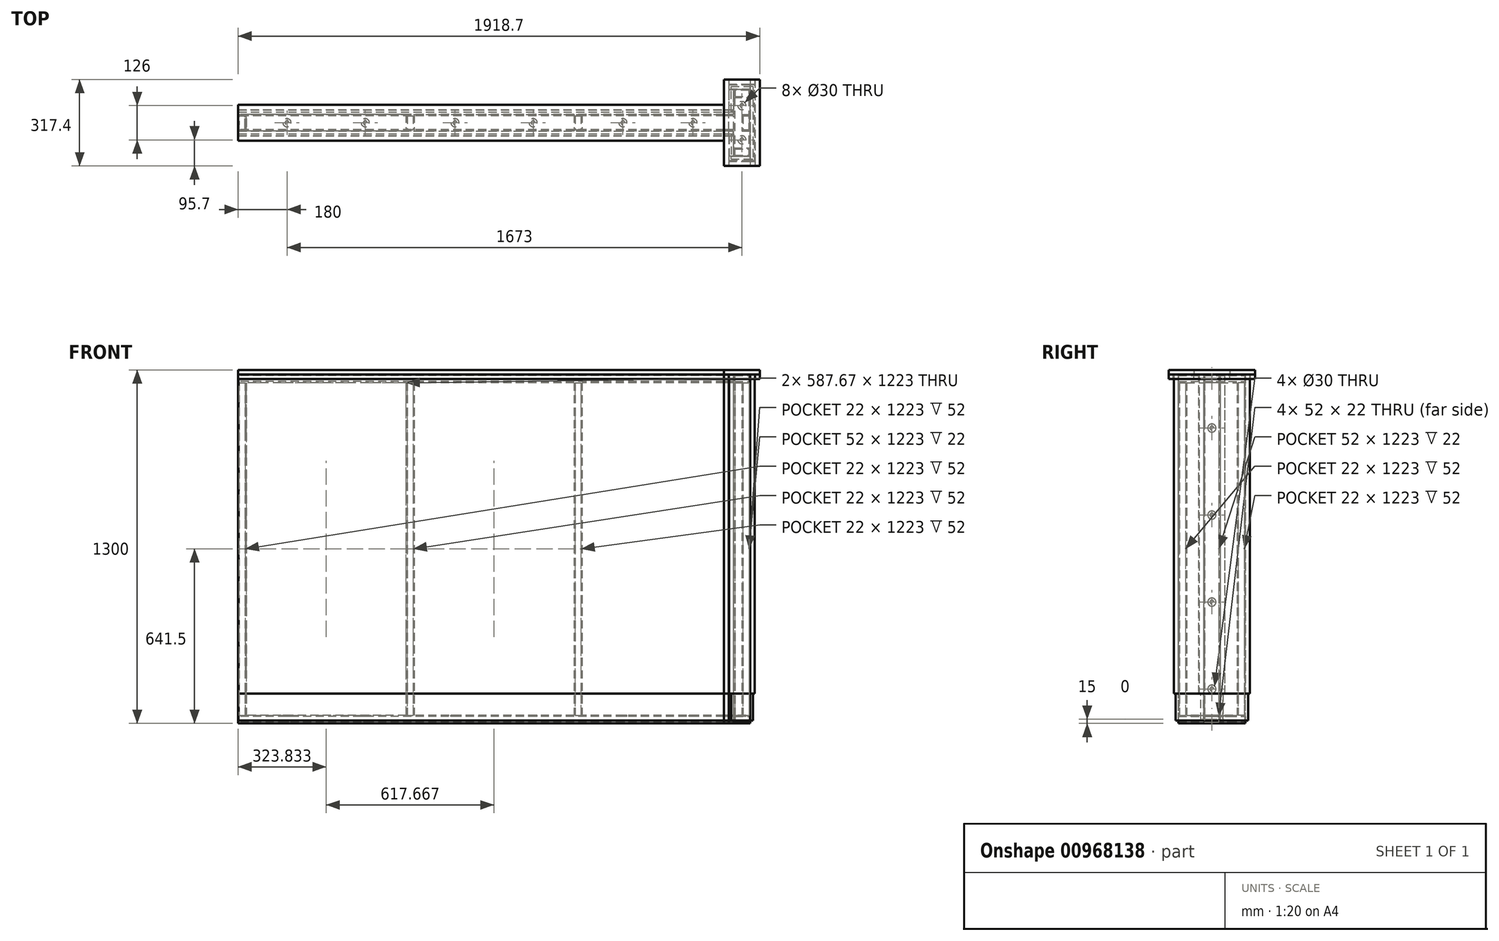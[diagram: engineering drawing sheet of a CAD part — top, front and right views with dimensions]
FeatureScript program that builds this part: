
annotation { "Feature Type Name" : "Feature", "Feature Type Description" : "" }
export const myFeature = defineFeature(function(context is Context, id is Id, definition is map)
    precondition{}
    {
        {
            var Q0;
            Q0=qCreatedBy(makeId("Right.planeOp"),FACE);
            var sketch = newSketch(context, id + "F0", { "sketchPlane" : qUnion([Q0])});
            skLineSegment(sketch, "E0.bottom", {"start": v(-30, 30) * mm, "end": v(30, 30) * mm});
            skLineSegment(sketch, "E0.top", {"start": v(-30, 0) * mm, "end": v(30, 0) * mm});
            skLineSegment(sketch, "E0.left", {"start": v(-30, 30) * mm, "end": v(-30, 0) * mm});
            skLineSegment(sketch, "E0.right", {"start": v(30, 30) * mm, "end": v(30, 0) * mm});
            skLineSegment(sketch, "E1.bottom", {"start": v(-26, 26) * mm, "end": v(26, 26) * mm});
            skLineSegment(sketch, "E1.top", {"start": v(-26, 4) * mm, "end": v(26, 4) * mm});
            skLineSegment(sketch, "E1.left", {"start": v(-26, 26) * mm, "end": v(-26, 4) * mm});
            skLineSegment(sketch, "E1.right", {"start": v(26, 26) * mm, "end": v(26, 4) * mm});
            skLineSegment(sketch, "E2.bottom", {"start": v(-30, 1283) * mm, "end": v(30, 1283) * mm});
            skLineSegment(sketch, "E2.top", {"start": v(-30, 1253) * mm, "end": v(30, 1253) * mm});
            skLineSegment(sketch, "E2.left", {"start": v(-30, 1283) * mm, "end": v(-30, 1253) * mm});
            skLineSegment(sketch, "E2.right", {"start": v(30, 1283) * mm, "end": v(30, 1253) * mm});
            skLineSegment(sketch, "E3.bottom", {"start": v(-26, 1279) * mm, "end": v(26, 1279) * mm});
            skLineSegment(sketch, "E3.top", {"start": v(-26, 1257) * mm, "end": v(26, 1257) * mm});
            skLineSegment(sketch, "E3.left", {"start": v(-26, 1279) * mm, "end": v(-26, 1257) * mm});
            skLineSegment(sketch, "E3.right", {"start": v(26, 1279) * mm, "end": v(26, 1257) * mm});
            skLineSegment(sketch, "E4", {"start": v(0, 1283) * mm, "end": v(0, 1279) * mm, "construction": true});
            skLineSegment(sketch, "E5", {"start": v(-30, 1268) * mm, "end": v(-26, 1268) * mm, "construction": true});
            skLineSegment(sketch, "E6", {"start": v(0, 1257) * mm, "end": v(0, 1253) * mm, "construction": true});
            skLineSegment(sketch, "E7", {"start": v(30, 1268) * mm, "end": v(26, 1268) * mm, "construction": true});
            skLineSegment(sketch, "E8", {"start": v(0, 30) * mm, "end": v(0, 26) * mm, "construction": true});
            skLineSegment(sketch, "E9", {"start": v(26, 15) * mm, "end": v(30, 15) * mm, "construction": true});
            skLineSegment(sketch, "E10", {"start": v(0, 0) * mm, "end": v(0, 4) * mm, "construction": true});
            skPoint(sketch, "E10.endSnap0", {"position": v(0, 4) * mm});
            skLineSegment(sketch, "E11", {"start": v(-26, 15) * mm, "end": v(-30, 15) * mm, "construction": true});
            skSolve(sketch);
        }
        {
            var Q0;
            Q0 = qSketchRegion(id + "F0", true);
            extrude(context, id + "F1", {"entities" : qUnion([Q0]), "depth" : (1900 - 17 - 60) * mm, "offsetDistance" : 25 * mm});
        }
        {
            var Q0;
            Q0=makeQuery(id+"F1.opExtrude","SWEPT_FACE",FACE,{"disambiguationData":[OSD([sQuery(id+"F0.wireOp",EDGE,"E0.bottom")])]});
            var sketch = newSketch(context, id + "F2", { "sketchPlane" : qUnion([Q0])});
            skLineSegment(sketch, "E12.bottom", {"start": v(0, -30) * mm, "end": v(30, -30) * mm});
            skLineSegment(sketch, "E12.top", {"start": v(0, 30) * mm, "end": v(30, 30) * mm});
            skLineSegment(sketch, "E12.left", {"start": v(0, -30) * mm, "end": v(0, 30) * mm});
            skLineSegment(sketch, "E12.right", {"start": v(30, -30) * mm, "end": v(30, 30) * mm});
            skLineSegment(sketch, "E13.bottom", {"start": v(4, -26) * mm, "end": v(26, -26) * mm});
            skLineSegment(sketch, "E13.top", {"start": v(4, 26) * mm, "end": v(26, 26) * mm});
            skLineSegment(sketch, "E13.left", {"start": v(4, -26) * mm, "end": v(4, 26) * mm});
            skLineSegment(sketch, "E13.right", {"start": v(26, -26) * mm, "end": v(26, 26) * mm});
            skLineSegment(sketch, "E14", {"start": v(15, -30) * mm, "end": v(15, -26) * mm, "construction": true});
            skLineSegment(sketch, "E15", {"start": v(30, 0) * mm, "end": v(26, 0) * mm, "construction": true});
            skLineSegment(sketch, "E16", {"start": v(15, 30) * mm, "end": v(15, 26) * mm, "construction": true});
            skLineSegment(sketch, "E17", {"start": v(4, 0) * mm, "end": v(0, 0) * mm, "construction": true});
            skSolve(sketch);
        }
        {
            var Q0;
            Q0 = qSketchRegion(id + "F2", true);
            extrude(context, id + "F3", {"entities" : qUnion([Q0]), "endBound" : BoundingType.UP_TO_NEXT, "depth" : 25 * mm, "offsetDistance" : 25 * mm});
        }
        {
            var Q0;
            Q0=qCreatedBy(makeId("Front.planeOp"),FACE);
            var sketch = newSketch(context, id + "F4", { "sketchPlane" : qUnion([Q0])});
            skLineSegment(sketch, "E18.bottom", {"start": v(1823, 1253) * mm, "end": v(1883, 1253) * mm});
            skLineSegment(sketch, "E18.top", {"start": v(1823, 1283) * mm, "end": v(1883, 1283) * mm});
            skLineSegment(sketch, "E18.left", {"start": v(1823, 1253) * mm, "end": v(1823, 1283) * mm});
            skLineSegment(sketch, "E18.right", {"start": v(1883, 1253) * mm, "end": v(1883, 1283) * mm});
            skLineSegment(sketch, "E19.bottom", {"start": v(1827, 1257) * mm, "end": v(1879, 1257) * mm});
            skLineSegment(sketch, "E19.top", {"start": v(1827, 1279) * mm, "end": v(1879, 1279) * mm});
            skLineSegment(sketch, "E19.left", {"start": v(1827, 1257) * mm, "end": v(1827, 1279) * mm});
            skLineSegment(sketch, "E19.right", {"start": v(1879, 1257) * mm, "end": v(1879, 1279) * mm});
            skLineSegment(sketch, "E20.bottom", {"start": v(1823, 30) * mm, "end": v(1883, 30) * mm});
            skLineSegment(sketch, "E20.top", {"start": v(1823, 0) * mm, "end": v(1883, 0) * mm});
            skLineSegment(sketch, "E20.left", {"start": v(1823, 30) * mm, "end": v(1823, 0) * mm});
            skLineSegment(sketch, "E20.right", {"start": v(1883, 30) * mm, "end": v(1883, 0) * mm});
            skLineSegment(sketch, "E21.bottom", {"start": v(1827, 26) * mm, "end": v(1879, 26) * mm});
            skLineSegment(sketch, "E21.top", {"start": v(1827, 4) * mm, "end": v(1879, 4) * mm});
            skLineSegment(sketch, "E21.left", {"start": v(1827, 26) * mm, "end": v(1827, 4) * mm});
            skLineSegment(sketch, "E21.right", {"start": v(1879, 26) * mm, "end": v(1879, 4) * mm});
            skLineSegment(sketch, "E22", {"start": v(1853, 30) * mm, "end": v(1853, 26) * mm, "construction": true});
            skLineSegment(sketch, "E23", {"start": v(1827, 15) * mm, "end": v(1823, 15) * mm, "construction": true});
            skLineSegment(sketch, "E24", {"start": v(1853, 4) * mm, "end": v(1853, 0) * mm, "construction": true});
            skLineSegment(sketch, "E25", {"start": v(1879, 15) * mm, "end": v(1883, 15) * mm, "construction": true});
            skLineSegment(sketch, "E26", {"start": v(1853, 1283) * mm, "end": v(1853, 1279) * mm, "construction": true});
            skLineSegment(sketch, "E27", {"start": v(1823, 1268) * mm, "end": v(1827, 1268) * mm, "construction": true});
            skLineSegment(sketch, "E28", {"start": v(1853, 1253) * mm, "end": v(1853, 1257) * mm, "construction": true});
            skPoint(sketch, "E28.startSnap0", {"position": v(1853, 1257) * mm});
            skLineSegment(sketch, "E29", {"start": v(1879, 1268) * mm, "end": v(1883, 1268) * mm, "construction": true});
            skSolve(sketch);
        }
        {
            var Q0;
            Q0 = qSketchRegion(id + "F4", true);
            extrude(context, id + "F5", {"entities" : qUnion([Q0]), "endBound" : BoundingType.SYMMETRIC, "depth" : (320 - 17 - 17 - 20 - 20) * mm, "offsetDistance" : 25 * mm});
        }
        {
            var Q0;
            Q0=makeQuery(id+"F5.opExtrude","SWEPT_FACE",FACE,{"disambiguationData":[OSD([sQuery(id+"F4.wireOp",EDGE,"E20.bottom")])]});
            var sketch = newSketch(context, id + "F6", { "sketchPlane" : qUnion([Q0])});
            skLineSegment(sketch, "E30.bottom", {"start": v(1883, 123) * mm, "end": v(1823, 123) * mm});
            skLineSegment(sketch, "E30.top", {"start": v(1883, 123) * mm, "end": v(1823, 123) * mm});
            skLineSegment(sketch, "E30.left", {"start": v(1883, 123) * mm, "end": v(1883, 123) * mm});
            skLineSegment(sketch, "E30.right", {"start": v(1823, 123) * mm, "end": v(1823, 123) * mm});
            skLineSegment(sketch, "E31.bottom", {"start": v(1823, 123) * mm, "end": v(1883, 123) * mm});
            skLineSegment(sketch, "E31.top", {"start": v(1823, 93) * mm, "end": v(1883, 93) * mm});
            skLineSegment(sketch, "E31.left", {"start": v(1823, 123) * mm, "end": v(1823, 93) * mm});
            skLineSegment(sketch, "E31.right", {"start": v(1883, 123) * mm, "end": v(1883, 93) * mm});
            skLineSegment(sketch, "E32.bottom", {"start": v(1883, -123) * mm, "end": v(1823, -123) * mm});
            skLineSegment(sketch, "E32.top", {"start": v(1883, -123) * mm, "end": v(1823, -123) * mm});
            skLineSegment(sketch, "E32.left", {"start": v(1883, -123) * mm, "end": v(1883, -123) * mm});
            skLineSegment(sketch, "E32.right", {"start": v(1823, -123) * mm, "end": v(1823, -123) * mm});
            skLineSegment(sketch, "E33.bottom", {"start": v(1823, -123) * mm, "end": v(1883, -123) * mm});
            skLineSegment(sketch, "E33.top", {"start": v(1823, -93) * mm, "end": v(1883, -93) * mm});
            skLineSegment(sketch, "E33.left", {"start": v(1823, -123) * mm, "end": v(1823, -93) * mm});
            skLineSegment(sketch, "E33.right", {"start": v(1883, -123) * mm, "end": v(1883, -93) * mm});
            skLineSegment(sketch, "E34.bottom", {"start": v(1853, 30) * mm, "end": v(1883, 30) * mm});
            skLineSegment(sketch, "E34.top", {"start": v(1853, -30) * mm, "end": v(1883, -30) * mm});
            skLineSegment(sketch, "E34.left", {"start": v(1853, 30) * mm, "end": v(1853, -30) * mm});
            skLineSegment(sketch, "E34.right", {"start": v(1883, 30) * mm, "end": v(1883, -30) * mm});
            skLineSegment(sketch, "E35.0", {"start": v(1857, 26) * mm, "end": v(1879, 26) * mm});
            skLineSegment(sketch, "E35.1", {"start": v(1857, 26) * mm, "end": v(1857, -26) * mm});
            skLineSegment(sketch, "E35.2", {"start": v(1857, -26) * mm, "end": v(1879, -26) * mm});
            skLineSegment(sketch, "E35.3", {"start": v(1879, 26) * mm, "end": v(1879, -26) * mm});
            skLineSegment(sketch, "E36.0", {"start": v(1879, 119) * mm, "end": v(1879, 97) * mm});
            skLineSegment(sketch, "E36.1", {"start": v(1879, 119) * mm, "end": v(1827, 119) * mm});
            skLineSegment(sketch, "E36.2", {"start": v(1827, 119) * mm, "end": v(1827, 97) * mm});
            skLineSegment(sketch, "E36.3", {"start": v(1827, 97) * mm, "end": v(1879, 97) * mm});
            skLineSegment(sketch, "E37.0", {"start": v(1827, -97) * mm, "end": v(1879, -97) * mm});
            skLineSegment(sketch, "E37.1", {"start": v(1827, -119) * mm, "end": v(1827, -97) * mm});
            skLineSegment(sketch, "E37.2", {"start": v(1827, -119) * mm, "end": v(1879, -119) * mm});
            skLineSegment(sketch, "E37.3", {"start": v(1879, -119) * mm, "end": v(1879, -97) * mm});
            skLineSegment(sketch, "E38.1.0.0", {"start": v(1235.33, 30) * mm, "end": v(1265.33, 30) * mm});
            skLineSegment(sketch, "E38.1.0.1", {"start": v(1235.33, 30) * mm, "end": v(1235.33, -30) * mm});
            skLineSegment(sketch, "E38.1.0.2", {"start": v(1235.33, -30) * mm, "end": v(1265.33, -30) * mm});
            skLineSegment(sketch, "E38.1.0.3", {"start": v(1239.33, 26) * mm, "end": v(1239.33, -26) * mm});
            skLineSegment(sketch, "E38.1.0.4", {"start": v(1239.33, 26) * mm, "end": v(1261.33, 26) * mm});
            skLineSegment(sketch, "E38.1.0.5", {"start": v(1265.33, 30) * mm, "end": v(1265.33, -30) * mm});
            skLineSegment(sketch, "E38.1.0.6", {"start": v(1261.33, 26) * mm, "end": v(1261.33, -26) * mm});
            skLineSegment(sketch, "E38.1.0.7", {"start": v(1239.33, -26) * mm, "end": v(1261.33, -26) * mm});
            skLineSegment(sketch, "E38.direction1", {"start": v(1853, 30) * mm, "end": v(1235.33, 30) * mm, "construction": true});
            skLineSegment(sketch, "E39.0.2.0", {"start": v(617.67, 30) * mm, "end": v(647.67, 30) * mm});
            skLineSegment(sketch, "E39.3.2.0", {"start": v(617.67, 30) * mm, "end": v(617.67, -30) * mm});
            skLineSegment(sketch, "E39.6.2.0", {"start": v(617.67, -30) * mm, "end": v(647.67, -30) * mm});
            skLineSegment(sketch, "E39.9.2.0", {"start": v(621.67, 26) * mm, "end": v(621.67, -26) * mm});
            skLineSegment(sketch, "E39.12.2.0", {"start": v(621.67, 26) * mm, "end": v(643.67, 26) * mm});
            skLineSegment(sketch, "E39.15.2.0", {"start": v(647.67, 30) * mm, "end": v(647.67, -30) * mm});
            skLineSegment(sketch, "E39.18.2.0", {"start": v(643.67, 26) * mm, "end": v(643.67, -26) * mm});
            skLineSegment(sketch, "E39.21.2.0", {"start": v(621.67, -26) * mm, "end": v(643.67, -26) * mm});
            skLineSegment(sketch, "E40", {"start": v(617.67, 0) * mm, "end": v(30, 0) * mm, "construction": true});
            skLineSegment(sketch, "E41", {"start": v(647.67, 0) * mm, "end": v(1235.33, 0) * mm, "construction": true});
            skLineSegment(sketch, "E42", {"start": v(1265.33, 0) * mm, "end": v(1853, 0) * mm, "construction": true});
            skSolve(sketch);
        }
        {
            var Q0;
            Q0 = qSketchRegion(id + "F6", true);
            extrude(context, id + "F7", {"entities" : qUnion([Q0]), "endBound" : BoundingType.UP_TO_NEXT, "depth" : 25 * mm, "offsetDistance" : 25 * mm});
        }
        {
            var Q0;
            Q0=makeQuery(id+"F1.opExtrude","SWEPT_FACE",FACE,{"disambiguationData":[OSD([sQuery(id+"F0.wireOp",EDGE,"E2.left")])]});
            cPlane(context, id + "F8", {"entities" : qUnion([Q0]), "cplaneType" : CPlaneType.OFFSET, "offset" : 0 * mm, "width" : 150 * mm, "height" : 150 * mm});
        }
        {
            var Q0;
            Q0=qCreatedBy(id+"F8.planeOp",FACE);
            var sketch = newSketch(context, id + "F9", { "sketchPlane" : qUnion([Q0])});
            skLineSegment(sketch, "E43.bottom", {"start": v(1.3, 1281.7) * mm, "end": v(1821.7, 1281.7) * mm});
            skLineSegment(sketch, "E43.top", {"start": v(1.3, 110) * mm, "end": v(1821.7, 110) * mm});
            skLineSegment(sketch, "E43.left", {"start": v(1.3, 1281.7) * mm, "end": v(1.3, 110) * mm});
            skLineSegment(sketch, "E43.right", {"start": v(1821.7, 1281.7) * mm, "end": v(1821.7, 110) * mm});
            skLineSegment(sketch, "E44", {"start": v(911.5, 1281.7) * mm, "end": v(911.5, 1283) * mm, "construction": true});
            skLineSegment(sketch, "E45", {"start": v(1821.7, 695.85) * mm, "end": v(1823, 695.85) * mm, "construction": true});
            skLineSegment(sketch, "E46", {"start": v(1.3, 641.5) * mm, "end": v(0, 641.5) * mm, "construction": true});
            skSolve(sketch);
        }
        {
            var Q0;
            Q0 = qSketchRegion(id + "F9", true);
            extrude(context, id + "F10", {"entities" : qUnion([Q0]), "depth" : 17 * mm, "offsetDistance" : 25 * mm});
        }
        {
            var Q0;
            Q0=qCreatedBy(id+"F8.planeOp",FACE);
            var sketch = newSketch(context, id + "F11", { "sketchPlane" : qUnion([Q0])});
            skLineSegment(sketch, "E47.bottom", {"start": v(1.3, 110) * mm, "end": v(1821.7, 110) * mm});
            skLineSegment(sketch, "E47.top", {"start": v(1.3, 10) * mm, "end": v(1821.7, 10) * mm});
            skLineSegment(sketch, "E47.left", {"start": v(1.3, 110) * mm, "end": v(1.3, 10) * mm});
            skLineSegment(sketch, "E47.right", {"start": v(1821.7, 110) * mm, "end": v(1821.7, 10) * mm});
            skSolve(sketch);
        }
        {
            var Q0;
            Q0 = qSketchRegion(id + "F11", true);
            extrude(context, id + "F12", {"entities" : qUnion([Q0]), "depth" : 10 * mm, "offsetDistance" : 25 * mm});
        }
        {
            var Q0;
            Q0=makeQuery(id+"F10.opExtrude","SWEPT_BODY",BODY,{"disambiguationData":[OSD([sQuery(id+"F9.wireOp",EDGE,"E43.bottom"),sQuery(id+"F9.wireOp",EDGE,"E43.top"),sQuery(id+"F9.wireOp",EDGE,"E43.left"),sQuery(id+"F9.wireOp",EDGE,"E43.right")])]});
            var Q1;
            Q1=makeQuery(id+"F12.opExtrude","SWEPT_BODY",BODY,{"disambiguationData":[OSD([sQuery(id+"F11.wireOp",EDGE,"E47.bottom"),sQuery(id+"F11.wireOp",EDGE,"E47.top"),sQuery(id+"F11.wireOp",EDGE,"E47.left"),sQuery(id+"F11.wireOp",EDGE,"E47.right")])]});
            var Q2;
            Q2=qCreatedBy(makeId("Front.planeOp"),FACE);
            mirror(context, id + "F13", {"entities" : qUnion([Q0, Q1]), "mirrorPlane" : qUnion([Q2])});
        }
        {
            var Q0;
            Q0=makeQuery(id+"F5.opExtrude","SWEPT_FACE",FACE,{"disambiguationData":[OSD([sQuery(id+"F4.wireOp",EDGE,"E18.top")])]});
            cPlane(context, id + "F14", {"entities" : qUnion([Q0]), "cplaneType" : CPlaneType.OFFSET, "offset" : 1.3 * mm, "oppositeDirection" : true, "width" : 150 * mm, "height" : 150 * mm});
        }
        {
            var Q0;
            Q0=qCreatedBy(id+"F14.planeOp",FACE);
            var sketch = newSketch(context, id + "F15", { "sketchPlane" : qUnion([Q0])});
            skLineSegment(sketch, "E48.bottom", {"start": v(1900, 140) * mm, "end": v(1883, 140) * mm});
            skLineSegment(sketch, "E48.top", {"start": v(1900, -140) * mm, "end": v(1883, -140) * mm});
            skLineSegment(sketch, "E48.left", {"start": v(1900, 140) * mm, "end": v(1900, -140) * mm});
            skLineSegment(sketch, "E48.right", {"start": v(1883, 123) * mm, "end": v(1883, -123) * mm});
            skLineSegment(sketch, "E49.bottom", {"start": v(1883, 140) * mm, "end": v(1806, 140) * mm});
            skLineSegment(sketch, "E49.top", {"start": v(1883, 123) * mm, "end": v(1806, 123) * mm});
            skLineSegment(sketch, "E49.right", {"start": v(1806, 140) * mm, "end": v(1806, 123) * mm});
            skLineSegment(sketch, "E50.bottom", {"start": v(1883, -123) * mm, "end": v(1806, -123) * mm});
            skLineSegment(sketch, "E50.top", {"start": v(1883, -140) * mm, "end": v(1806, -140) * mm});
            skLineSegment(sketch, "E50.right", {"start": v(1806, -123) * mm, "end": v(1806, -140) * mm});
            skSolve(sketch);
        }
        {
            var Q0;
            Q0=makeQuery(id+"F15.imprint","IMPRINT",FACE,{"disambiguationData":[TD([[makeQuery(id+"F15.imprint","IMPRINT",EDGE,{"derivedFrom":sQuery(id+"F15.wireOp",EDGE,"E48.bottom")}),1.0]])]});
            var Q1;
            Q1=makeQuery(id+"F10.opExtrude","SWEPT_FACE",FACE,{"disambiguationData":[OSD([sQuery(id+"F9.wireOp",EDGE,"E43.top")])]});
            extrude(context, id + "F16", {"entities" : qUnion([Q0]), "endBound" : BoundingType.UP_TO_SURFACE, "oppositeDirection" : true, "depth" : 25 * mm, "endBoundEntityFace" : qUnion([Q1]), "offsetDistance" : 25 * mm});
        }
        {
            var Q0;
            Q0=makeQuery(id+"F16.opExtrude","CAP_FACE",FACE,{"disambiguationData":[OSD([sQuery(id+"F15.wireOp",EDGE,"E48.bottom"),sQuery(id+"F15.wireOp",EDGE,"E48.top"),sQuery(id+"F15.wireOp",EDGE,"E48.left"),sQuery(id+"F15.wireOp",EDGE,"E48.right"),sQuery(id+"F15.wireOp",EDGE,"E49.bottom"),sQuery(id+"F15.wireOp",EDGE,"E49.top"),sQuery(id+"F15.wireOp",EDGE,"E49.right"),sQuery(id+"F15.wireOp",EDGE,"E50.bottom"),sQuery(id+"F15.wireOp",EDGE,"E50.top"),sQuery(id+"F15.wireOp",EDGE,"E50.right")])],"isStart":false});
            var sketch = newSketch(context, id + "F17", { "sketchPlane" : qUnion([Q0])});
            skLineSegment(sketch, "E51", {"start": v(1813, -123) * mm, "end": v(1883, -123) * mm});
            skLineSegment(sketch, "E52", {"start": v(1883, -123) * mm, "end": v(1883, 123) * mm});
            skLineSegment(sketch, "E53", {"start": v(1883, 123) * mm, "end": v(1813, 123) * mm});
            skLineSegment(sketch, "E54", {"start": v(1813, 133) * mm, "end": v(1893, 133) * mm});
            skLineSegment(sketch, "E55", {"start": v(1893, 133) * mm, "end": v(1893, -133) * mm});
            skLineSegment(sketch, "E56", {"start": v(1893, -133) * mm, "end": v(1813, -133) * mm});
            skLineSegment(sketch, "E57", {"start": v(1813, -133) * mm, "end": v(1813, -123) * mm});
            skLineSegment(sketch, "E58", {"start": v(1813, 123) * mm, "end": v(1813, 133) * mm});
            skPoint(sketch, "E59.orphan", {"position": v(1806, -133) * mm});
            skPoint(sketch, "E60.orphan", {"position": v(1806, 123) * mm});
            skSolve(sketch);
        }
        {
            var Q0;
            Q0=makeQuery(id+"F17.imprint","IMPRINT",FACE,{"disambiguationData":[TD([[makeQuery(id+"F17.imprint","IMPRINT",EDGE,{"derivedFrom":sQuery(id+"F17.wireOp",EDGE,"E51")}),-1.0]])]});
            var Q1;
            Q1=makeQuery(id+"F12.opExtrude","SWEPT_FACE",FACE,{"disambiguationData":[OSD([sQuery(id+"F11.wireOp",EDGE,"E47.top")])]});
            extrude(context, id + "F18", {"entities" : qUnion([Q0]), "endBound" : BoundingType.UP_TO_SURFACE, "depth" : 25 * mm, "endBoundEntityFace" : qUnion([Q1]), "offsetDistance" : 25 * mm});
        }
        {
            var Q0;
            Q0=makeQuery(id+"F5.opExtrude","SWEPT_FACE",FACE,{"disambiguationData":[OSD([sQuery(id+"F4.wireOp",EDGE,"E18.top")])]});
            var sketch = newSketch(context, id + "F19", { "sketchPlane" : qUnion([Q0])});
            skLineSegment(sketch, "E61.bottom", {"start": v(1823, -121.7) * mm, "end": v(1806, -121.7) * mm});
            skLineSegment(sketch, "E61.top", {"start": v(1823, -48.3) * mm, "end": v(1806, -48.3) * mm});
            skLineSegment(sketch, "E61.left", {"start": v(1823, -121.7) * mm, "end": v(1823, -48.3) * mm});
            skLineSegment(sketch, "E61.right", {"start": v(1806, -121.7) * mm, "end": v(1806, -48.3) * mm});
            skLineSegment(sketch, "E62.MirrorCS", {"start": v(1823, 48.3) * mm, "end": v(1806, 48.3) * mm});
            skLineSegment(sketch, "E63.MirrorCS", {"start": v(1823, 121.7) * mm, "end": v(1806, 121.7) * mm});
            skLineSegment(sketch, "E64.MirrorCS", {"start": v(1806, 121.7) * mm, "end": v(1806, 48.3) * mm});
            skLineSegment(sketch, "E65.MirrorCS", {"start": v(1823, 121.7) * mm, "end": v(1823, 48.3) * mm});
            skSolve(sketch);
        }
        {
            var Q0;
            Q0 = qSketchRegion(id + "F19", true);
            var Q1;
            Q1=makeQuery(id+"F10.opExtrude","SWEPT_FACE",FACE,{"disambiguationData":[OSD([sQuery(id+"F9.wireOp",EDGE,"E43.top")])]});
            extrude(context, id + "F20", {"entities" : qUnion([Q0]), "endBound" : BoundingType.UP_TO_SURFACE, "oppositeDirection" : true, "depth" : 25 * mm, "endBoundEntityFace" : qUnion([Q1]), "offsetDistance" : 25 * mm});
        }
        {
            var Q0;
            Q0=makeQuery(id+"F20.opExtrude","CAP_FACE",FACE,{"disambiguationData":[OSD([sQuery(id+"F19.wireOp",EDGE,"E62.MirrorCS"),sQuery(id+"F19.wireOp",EDGE,"E63.MirrorCS"),sQuery(id+"F19.wireOp",EDGE,"E64.MirrorCS"),sQuery(id+"F19.wireOp",EDGE,"E65.MirrorCS")])],"isStart":false});
            var sketch = newSketch(context, id + "F21", { "sketchPlane" : qUnion([Q0])});
            skLineSegment(sketch, "E66.bottom", {"start": v(1823, -121.7) * mm, "end": v(1813, -121.7) * mm});
            skLineSegment(sketch, "E66.top", {"start": v(1823, -41.3) * mm, "end": v(1813, -41.3) * mm});
            skLineSegment(sketch, "E66.left", {"start": v(1823, -121.7) * mm, "end": v(1823, -41.3) * mm});
            skLineSegment(sketch, "E66.right", {"start": v(1813, -121.7) * mm, "end": v(1813, -41.3) * mm});
            skLineSegment(sketch, "E67.bottom", {"start": v(1823, 121.7) * mm, "end": v(1813, 121.7) * mm});
            skLineSegment(sketch, "E67.top", {"start": v(1823, 41.3) * mm, "end": v(1813, 41.3) * mm});
            skLineSegment(sketch, "E67.left", {"start": v(1823, 121.7) * mm, "end": v(1823, 41.3) * mm});
            skLineSegment(sketch, "E67.right", {"start": v(1813, 121.7) * mm, "end": v(1813, 41.3) * mm});
            skSolve(sketch);
        }
        {
            var Q0;
            {var subQ0=sQuery(id+"F21.wireOp",EDGE,"E66.top");Q0=makeQuery(id+"F21.imprint","IMPRINT",FACE,{"disambiguationData":[TD([[makeQuery(id+"F21.imprint","IMPRINT",EDGE,{"derivedFrom":subQ0}),1.0]])]});}
            var Q1;
            {var subQ0=sQuery(id+"F21.wireOp",EDGE,"E66.bottom");Q1=makeQuery(id+"F21.imprint","IMPRINT",FACE,{"disambiguationData":[TD([[makeQuery(id+"F21.imprint","IMPRINT",EDGE,{"derivedFrom":subQ0}),1.0]])]});}
            var Q2;
            Q2=makeQuery(id+"F21.imprint","IMPRINT",FACE,{"disambiguationData":[TD([[makeQuery(id+"F21.imprint","IMPRINT",EDGE,{"derivedFrom":sQuery(id+"F21.wireOp",EDGE,"E67.bottom")}),1.0]])]});
            var Q3;
            Q3=makeQuery(id+"F12.opExtrude","SWEPT_FACE",FACE,{"disambiguationData":[OSD([sQuery(id+"F11.wireOp",EDGE,"E47.top")])]});
            extrude(context, id + "F22", {"entities" : qUnion([Q0, Q1, Q2]), "endBound" : BoundingType.UP_TO_SURFACE, "depth" : 25 * mm, "endBoundEntityFace" : qUnion([Q3]), "offsetDistance" : 25 * mm});
        }
        {
            var Q0;
            Q0=makeQuery(id+"F1.opExtrude","SWEPT_FACE",FACE,{"disambiguationData":[OSD([sQuery(id+"F0.wireOp",EDGE,"E2.bottom")])]});
            var sketch = newSketch(context, id + "F23", { "sketchPlane" : qUnion([Q0])});
            skLineSegment(sketch, "E68.bottom", {"start": v(0, 65.7) * mm, "end": v(1787.13, 65.7) * mm});
            skLineSegment(sketch, "E68.top", {"start": v(0, -65.7) * mm, "end": v(1787.13, -65.7) * mm});
            skLineSegment(sketch, "E68.left", {"start": v(0, 65.7) * mm, "end": v(0, -65.7) * mm});
            skLineSegment(sketch, "E68.right", {"start": v(1787.13, 65.7) * mm, "end": v(1787.13, -65.7) * mm});
            skSolve(sketch);
        }
        {
            var Q0;
            Q0 = qSketchRegion(id + "F23", true);
            extrude(context, id + "F24", {"entities" : qUnion([Q0]), "depth" : 17 * mm, "offsetDistance" : 25 * mm});
        }
        {
            var Q0;
            Q0=makeQuery(id+"F1.opExtrude","SWEPT_FACE",FACE,{"disambiguationData":[OSD([sQuery(id+"F0.wireOp",EDGE,"E2.bottom")])]});
            var sketch = newSketch(context, id + "F25", { "sketchPlane" : qUnion([Q0])});
            skLineSegment(sketch, "E69.bottom", {"start": v(1787.3, 158.7) * mm, "end": v(1918.7, 158.7) * mm});
            skLineSegment(sketch, "E69.top", {"start": v(1787.3, -158.7) * mm, "end": v(1918.7, -158.7) * mm});
            skLineSegment(sketch, "E69.left", {"start": v(1787.3, 158.7) * mm, "end": v(1787.3, -158.7) * mm});
            skLineSegment(sketch, "E69.right", {"start": v(1918.7, 158.7) * mm, "end": v(1918.7, -158.7) * mm});
            skPoint(sketch, "E70", {"position": v(1787.3, 0) * mm});
            skLineSegment(sketch, "E71", {"start": v(1787.3, 0) * mm, "end": v(1787.13, 0) * mm, "construction": true});
            skSolve(sketch);
        }
        {
            var Q0;
            {var subQ7=sQuery(id+"F25.wireOp",EDGE,"E69.bottom");Q0=makeQuery(id+"F25.imprint","IMPRINT",FACE,{"disambiguationData":[TD([[makeQuery(id+"F25.imprint","IMPRINT",EDGE,{"derivedFrom":subQ7}),-1.0]])]});}
            var Q1;
            {var subQ1=sQuery(id+"F0.wireOp",EDGE,"E2.bottom");var subQ9=makeQuery(id+"F1.opExtrude","CAP_EDGE",EDGE,{"disambiguationData":[OSD([subQ1])],"isStart":false});Q1=makeQuery(id+"F25.imprint","IMPRINT",FACE,{"disambiguationData":[TD([[makeQuery(id+"F25.imprint","IMPRINT",EDGE,{"derivedFrom":subQ9}),1.0]])]});}
            extrude(context, id + "F26", {"entities" : qUnion([Q0, Q1]), "depth" : 17 * mm, "offsetDistance" : 25 * mm});
        }
        {
            var Q0;
            {var subQ0=sQuery(id+"F23.wireOp",EDGE,"E68.top");var subQ1=sQuery(id+"F0.wireOp",EDGE,"E2.left");var subQ3=sQuery(id+"F23.wireOp",EDGE,"E68.left");var subQ4=sQuery(id+"F23.wireOp",EDGE,"E68.right");Q0=makeQuery(id+"F24.boolean.opBoolean","SPLIT",FACE,{"disambiguationData":[TD([makeQuery(id+"F1.opExtrude","SWEPT_FACE",FACE,{"disambiguationData":[OSD([subQ1])]})])],"derivedFrom":makeQuery(id+"F24.opExtrude","CAP_FACE",FACE,{"disambiguationData":[OSD([sQuery(id+"F23.wireOp",EDGE,"E68.bottom"),subQ0,subQ3,subQ4])],"isStart":true})});}
            var sketch = newSketch(context, id + "F27", { "sketchPlane" : qUnion([Q0])});
            skLineSegment(sketch, "E72.bottom", {"start": v(0, -65.7) * mm, "end": v(1804.3, -65.7) * mm});
            skLineSegment(sketch, "E72.top", {"start": v(0, -48.7) * mm, "end": v(1804.3, -48.7) * mm});
            skLineSegment(sketch, "E72.left", {"start": v(0, -65.7) * mm, "end": v(0, -48.7) * mm});
            skLineSegment(sketch, "E72.right", {"start": v(1804.3, -65.7) * mm, "end": v(1804.3, -48.7) * mm});
            skLineSegment(sketch, "E73", {"start": v(0, 0) * mm, "end": v(382.2, 0) * mm, "construction": true});
            skLineSegment(sketch, "E74.MirrorCS", {"start": v(0, 65.7) * mm, "end": v(0, 48.7) * mm});
            skLineSegment(sketch, "E75.MirrorCS", {"start": v(1804.3, 65.7) * mm, "end": v(1804.3, 48.7) * mm});
            skLineSegment(sketch, "E76.MirrorCS", {"start": v(0, 48.7) * mm, "end": v(1804.3, 48.7) * mm});
            skLineSegment(sketch, "E77.MirrorCS", {"start": v(0, 65.7) * mm, "end": v(1804.3, 65.7) * mm});
            skLineSegment(sketch, "E78.bottom", {"start": v(1787.3, -158.7) * mm, "end": v(1804.3, -158.7) * mm});
            skLineSegment(sketch, "E78.top", {"start": v(1787.3, -65.7) * mm, "end": v(1804.3, -65.7) * mm});
            skLineSegment(sketch, "E78.left", {"start": v(1787.3, -158.7) * mm, "end": v(1787.3, -65.7) * mm});
            skLineSegment(sketch, "E78.right", {"start": v(1804.3, -158.7) * mm, "end": v(1804.3, -65.7) * mm});
            skLineSegment(sketch, "E79.bottom", {"start": v(1804.3, -141.7) * mm, "end": v(1901.7, -141.7) * mm});
            skLineSegment(sketch, "E79.top", {"start": v(1804.3, -158.7) * mm, "end": v(1918.7, -158.7) * mm});
            skLineSegment(sketch, "E79.left", {"start": v(1804.3, -141.7) * mm, "end": v(1804.3, -158.7) * mm});
            skLineSegment(sketch, "E79.right", {"start": v(1918.7, -141.7) * mm, "end": v(1918.7, -158.7) * mm});
            skLineSegment(sketch, "E80.MirrorCS", {"start": v(1787.3, 65.7) * mm, "end": v(1804.3, 65.7) * mm});
            skLineSegment(sketch, "E81.MirrorCS", {"start": v(1918.7, 141.7) * mm, "end": v(1918.7, 158.7) * mm});
            skLineSegment(sketch, "E82.MirrorCS", {"start": v(1804.3, 158.7) * mm, "end": v(1918.7, 158.7) * mm});
            skLineSegment(sketch, "E83.MirrorCS", {"start": v(1787.3, 158.7) * mm, "end": v(1787.3, 65.7) * mm});
            skLineSegment(sketch, "E84.MirrorCS", {"start": v(1804.3, 158.7) * mm, "end": v(1804.3, 65.7) * mm});
            skLineSegment(sketch, "E85.MirrorCS", {"start": v(1804.3, 141.7) * mm, "end": v(1804.3, 158.7) * mm});
            skLineSegment(sketch, "E86.MirrorCS", {"start": v(1804.3, 141.7) * mm, "end": v(1901.7, 141.7) * mm});
            skLineSegment(sketch, "E87.MirrorCS", {"start": v(1787.3, 158.7) * mm, "end": v(1804.3, 158.7) * mm});
            skLineSegment(sketch, "E88.left", {"start": v(1918.7, -141.7) * mm, "end": v(1918.7, 141.7) * mm});
            skLineSegment(sketch, "E88.right", {"start": v(1901.7, -141.7) * mm, "end": v(1901.7, 141.7) * mm});
            skSolve(sketch);
        }
        {
            var Q0;
            Q0 = qSketchRegion(id + "F27", true);
            extrude(context, id + "F28", {"entities" : qUnion([Q0]), "depth" : 17 * mm, "offsetDistance" : 25 * mm});
        }
        {
            var Q0;
            Q0=makeQuery(id+"F1.opExtrude","SWEPT_BODY",BODY,{"disambiguationData":[OSD([sQuery(id+"F0.wireOp",EDGE,"E0.bottom"),sQuery(id+"F0.wireOp",EDGE,"E0.top"),sQuery(id+"F0.wireOp",EDGE,"E0.left"),sQuery(id+"F0.wireOp",EDGE,"E0.right"),sQuery(id+"F0.wireOp",EDGE,"E1.bottom"),sQuery(id+"F0.wireOp",EDGE,"E1.top"),sQuery(id+"F0.wireOp",EDGE,"E1.left"),sQuery(id+"F0.wireOp",EDGE,"E1.right")])]});
            var Q1;
            Q1=makeQuery(id+"F1.opExtrude","SWEPT_BODY",BODY,{"disambiguationData":[OSD([sQuery(id+"F0.wireOp",EDGE,"E2.bottom"),sQuery(id+"F0.wireOp",EDGE,"E2.top"),sQuery(id+"F0.wireOp",EDGE,"E2.left"),sQuery(id+"F0.wireOp",EDGE,"E2.right"),sQuery(id+"F0.wireOp",EDGE,"E3.bottom"),sQuery(id+"F0.wireOp",EDGE,"E3.top"),sQuery(id+"F0.wireOp",EDGE,"E3.left"),sQuery(id+"F0.wireOp",EDGE,"E3.right")])]});
            var Q2;
            Q2=makeQuery(id+"F3.opExtrude","SWEPT_BODY",BODY,{"disambiguationData":[OSD([sQuery(id+"F2.wireOp",EDGE,"E12.bottom"),sQuery(id+"F2.wireOp",EDGE,"E12.top"),sQuery(id+"F2.wireOp",EDGE,"E12.left"),sQuery(id+"F2.wireOp",EDGE,"E12.right"),sQuery(id+"F2.wireOp",EDGE,"E13.bottom"),sQuery(id+"F2.wireOp",EDGE,"E13.top"),sQuery(id+"F2.wireOp",EDGE,"E13.left"),sQuery(id+"F2.wireOp",EDGE,"E13.right")])]});
            var Q3;
            Q3=makeQuery(id+"F5.opExtrude","SWEPT_BODY",BODY,{"disambiguationData":[OSD([sQuery(id+"F4.wireOp",EDGE,"E18.bottom"),sQuery(id+"F4.wireOp",EDGE,"E18.top"),sQuery(id+"F4.wireOp",EDGE,"E18.left"),sQuery(id+"F4.wireOp",EDGE,"E18.right"),sQuery(id+"F4.wireOp",EDGE,"E19.bottom"),sQuery(id+"F4.wireOp",EDGE,"E19.top"),sQuery(id+"F4.wireOp",EDGE,"E19.left"),sQuery(id+"F4.wireOp",EDGE,"E19.right")])]});
            var Q4;
            Q4=makeQuery(id+"F5.opExtrude","SWEPT_BODY",BODY,{"disambiguationData":[OSD([sQuery(id+"F4.wireOp",EDGE,"E20.bottom"),sQuery(id+"F4.wireOp",EDGE,"E20.top"),sQuery(id+"F4.wireOp",EDGE,"E20.left"),sQuery(id+"F4.wireOp",EDGE,"E20.right"),sQuery(id+"F4.wireOp",EDGE,"E21.bottom"),sQuery(id+"F4.wireOp",EDGE,"E21.top"),sQuery(id+"F4.wireOp",EDGE,"E21.left"),sQuery(id+"F4.wireOp",EDGE,"E21.right")])]});
            var Q5;
            Q5=makeQuery(id+"F7.opExtrude","SWEPT_BODY",BODY,{"disambiguationData":[OSD([sQuery(id+"F6.wireOp",EDGE,"E31.bottom"),sQuery(id+"F6.wireOp",EDGE,"E31.top"),sQuery(id+"F6.wireOp",EDGE,"E31.left"),sQuery(id+"F6.wireOp",EDGE,"E31.right"),sQuery(id+"F6.wireOp",EDGE,"E36.0"),sQuery(id+"F6.wireOp",EDGE,"E36.1"),sQuery(id+"F6.wireOp",EDGE,"E36.2"),sQuery(id+"F6.wireOp",EDGE,"E36.3")])]});
            var Q6;
            Q6=makeQuery(id+"F7.opExtrude","SWEPT_BODY",BODY,{"disambiguationData":[OSD([sQuery(id+"F6.wireOp",EDGE,"E33.bottom"),sQuery(id+"F6.wireOp",EDGE,"E33.top"),sQuery(id+"F6.wireOp",EDGE,"E33.left"),sQuery(id+"F6.wireOp",EDGE,"E33.right"),sQuery(id+"F6.wireOp",EDGE,"E37.0"),sQuery(id+"F6.wireOp",EDGE,"E37.1"),sQuery(id+"F6.wireOp",EDGE,"E37.2"),sQuery(id+"F6.wireOp",EDGE,"E37.3")])]});
            var Q7;
            Q7=makeQuery(id+"F7.opExtrude","SWEPT_BODY",BODY,{"disambiguationData":[OSD([sQuery(id+"F6.wireOp",EDGE,"E34.bottom"),sQuery(id+"F6.wireOp",EDGE,"E34.top"),sQuery(id+"F6.wireOp",EDGE,"E34.left"),sQuery(id+"F6.wireOp",EDGE,"E34.right"),sQuery(id+"F6.wireOp",EDGE,"E35.0"),sQuery(id+"F6.wireOp",EDGE,"E35.1"),sQuery(id+"F6.wireOp",EDGE,"E35.2"),sQuery(id+"F6.wireOp",EDGE,"E35.3")])]});
            var Q8;
            Q8=makeQuery(id+"F7.opExtrude","SWEPT_BODY",BODY,{"disambiguationData":[OSD([sQuery(id+"F6.wireOp",EDGE,"E38.1.0.0"),sQuery(id+"F6.wireOp",EDGE,"E38.1.0.1"),sQuery(id+"F6.wireOp",EDGE,"E38.1.0.2"),sQuery(id+"F6.wireOp",EDGE,"E38.1.0.3"),sQuery(id+"F6.wireOp",EDGE,"E38.1.0.4"),sQuery(id+"F6.wireOp",EDGE,"E38.1.0.5"),sQuery(id+"F6.wireOp",EDGE,"E38.1.0.6"),sQuery(id+"F6.wireOp",EDGE,"E38.1.0.7")])]});
            var Q9;
            Q9=makeQuery(id+"F7.opExtrude","SWEPT_BODY",BODY,{"disambiguationData":[OSD([sQuery(id+"F6.wireOp",EDGE,"E39.0.2.0"),sQuery(id+"F6.wireOp",EDGE,"E39.3.2.0"),sQuery(id+"F6.wireOp",EDGE,"E39.6.2.0"),sQuery(id+"F6.wireOp",EDGE,"E39.9.2.0"),sQuery(id+"F6.wireOp",EDGE,"E39.12.2.0"),sQuery(id+"F6.wireOp",EDGE,"E39.15.2.0"),sQuery(id+"F6.wireOp",EDGE,"E39.18.2.0"),sQuery(id+"F6.wireOp",EDGE,"E39.21.2.0")])]});
            booleanBodies(context, id + "F29", {"operationType" : BooleanOperationType.UNION, "tools" : qUnion([Q0, Q1, Q2, Q3, Q4, Q5, Q6, Q7, Q8, Q9])});
        }
        {
            var Q0;
            Q0=makeQuery(id+"F29.opBoolean","SPLIT",FACE,{"disambiguationData":[TD([makeQuery(id+"F7.opExtrude","SWEPT_FACE",FACE,{"disambiguationData":[OSD([sQuery(id+"F6.wireOp",EDGE,"E38.1.0.1")])]})])],"derivedFrom":makeQuery(id+"F1.opExtrude","SWEPT_FACE",FACE,{"disambiguationData":[OSD([sQuery(id+"F0.wireOp",EDGE,"E0.bottom")])]})});
            var sketch = newSketch(context, id + "F30", { "sketchPlane" : qUnion([Q0])});
            skLineSegment(sketch, "E89", {"start": v(0, 0) * mm, "end": v(1853, 0) * mm, "construction": true});
            skLineSegment(sketch, "E90", {"start": v(1853, 123) * mm, "end": v(1853, -123) * mm, "construction": true});
            skCircle(sketch, "E91", {"center": v(1853, 63) * mm, "radius": 15 * mm});
            skCircle(sketch, "E92", {"center": v(1853, -63) * mm, "radius": 15 * mm});
            skCircle(sketch, "E93", {"center": v(180, 0) * mm, "radius": 15 * mm});
            skCircle(sketch, "E94", {"center": v(467.67, 0) * mm, "radius": 15 * mm});
            skCircle(sketch, "E95", {"center": v(797.67, 0) * mm, "radius": 15 * mm});
            skCircle(sketch, "E96", {"center": v(1085.33, 0) * mm, "radius": 15 * mm});
            skCircle(sketch, "E97", {"center": v(1415.33, 0) * mm, "radius": 15 * mm});
            skCircle(sketch, "E98", {"center": v(1673, 0) * mm, "radius": 15 * mm});
            skSolve(sketch);
        }
        {
            var Q0;
            Q0 = qSketchRegion(id + "F30", true);
            extrude(context, id + "F31", {"entities" : qUnion([Q0]), "operationType" : NewBodyOperationType.REMOVE, "oppositeDirection" : true, "depth" : 10 * mm, "offsetDistance" : 25 * mm});
        }
        {
            var Q0;
            Q0=makeQuery(id+"F29.opBoolean","SPLIT",FACE,{"disambiguationData":[TD([makeQuery(id+"F3.opExtrude","SWEPT_FACE",FACE,{"disambiguationData":[OSD([sQuery(id+"F2.wireOp",EDGE,"E12.right")])]})])],"derivedFrom":makeQuery(id+"F1.opExtrude","SWEPT_FACE",FACE,{"disambiguationData":[OSD([sQuery(id+"F0.wireOp",EDGE,"E0.bottom")])]})});
            var sketch = newSketch(context, id + "F32", { "sketchPlane" : qUnion([Q0])});
            skCircle(sketch, "E99", {"center": v(180, 0) * mm, "radius": 7 * mm});
            skCircle(sketch, "E100", {"center": v(467.67, 0) * mm, "radius": 7 * mm});
            skCircle(sketch, "E101", {"center": v(797.67, 0) * mm, "radius": 7 * mm});
            skCircle(sketch, "E102", {"center": v(1085.33, 0) * mm, "radius": 7 * mm});
            skCircle(sketch, "E103", {"center": v(1415.33, 0) * mm, "radius": 7 * mm});
            skCircle(sketch, "E104", {"center": v(1673, 0) * mm, "radius": 7 * mm});
            skCircle(sketch, "E105", {"center": v(1853, 63) * mm, "radius": 7 * mm});
            skCircle(sketch, "E106", {"center": v(1853, -63) * mm, "radius": 7 * mm});
            skSolve(sketch);
        }
        {
            var Q0;
            Q0 = qSketchRegion(id + "F32", true);
            extrude(context, id + "F33", {"entities" : qUnion([Q0]), "operationType" : NewBodyOperationType.REMOVE, "endBound" : BoundingType.THROUGH_ALL, "oppositeDirection" : true, "depth" : 25 * mm, "offsetDistance" : 25 * mm});
        }
        {
            var Q0;
            Q0=makeQuery(id+"F29.opBoolean","MERGE",FACE,{"derivedFrom":[makeQuery(id+"F1.opExtrude","CAP_FACE",FACE,{"disambiguationData":[OSD([sQuery(id+"F0.wireOp",EDGE,"E0.bottom"),sQuery(id+"F0.wireOp",EDGE,"E0.top"),sQuery(id+"F0.wireOp",EDGE,"E0.left"),sQuery(id+"F0.wireOp",EDGE,"E0.right"),sQuery(id+"F0.wireOp",EDGE,"E1.bottom"),sQuery(id+"F0.wireOp",EDGE,"E1.top"),sQuery(id+"F0.wireOp",EDGE,"E1.left"),sQuery(id+"F0.wireOp",EDGE,"E1.right")])],"isStart":true}),makeQuery(id+"F1.opExtrude","CAP_FACE",FACE,{"disambiguationData":[OSD([sQuery(id+"F0.wireOp",EDGE,"E2.bottom"),sQuery(id+"F0.wireOp",EDGE,"E2.top"),sQuery(id+"F0.wireOp",EDGE,"E2.left"),sQuery(id+"F0.wireOp",EDGE,"E2.right"),sQuery(id+"F0.wireOp",EDGE,"E3.bottom"),sQuery(id+"F0.wireOp",EDGE,"E3.top"),sQuery(id+"F0.wireOp",EDGE,"E3.left"),sQuery(id+"F0.wireOp",EDGE,"E3.right")])],"isStart":true}),makeQuery(id+"F3.opExtrude","SWEPT_FACE",FACE,{"disambiguationData":[OSD([sQuery(id+"F2.wireOp",EDGE,"E12.left")])]})]});
            var sketch = newSketch(context, id + "F34", { "sketchPlane" : qUnion([Q0])});
            skLineSegment(sketch, "E107", {"start": v(0, 26) * mm, "end": v(0, 1253) * mm, "construction": true});
            skCircle(sketch, "E108", {"center": v(0, 126) * mm, "radius": 7 * mm});
            skCircle(sketch, "E109.0.1.0", {"center": v(0, 446) * mm, "radius": 7 * mm});
            skLineSegment(sketch, "E109.0.1.1", {"start": v(0, 346) * mm, "end": v(0, 1573) * mm, "construction": true});
            skCircle(sketch, "E109.0.2.0", {"center": v(0, 766) * mm, "radius": 7 * mm});
            skLineSegment(sketch, "E109.0.2.1", {"start": v(0, 666) * mm, "end": v(0, 1893) * mm, "construction": true});
            skCircle(sketch, "E109.0.3.0", {"center": v(0, 1086) * mm, "radius": 7 * mm});
            skLineSegment(sketch, "E109.0.3.1", {"start": v(0, 986) * mm, "end": v(0, 2213) * mm, "construction": true});
            skCircle(sketch, "E109.0.4.0", {"center": v(0, 1406) * mm, "radius": 7 * mm});
            skLineSegment(sketch, "E109.0.4.1", {"start": v(0, 1306) * mm, "end": v(0, 2533) * mm, "construction": true});
            skLineSegment(sketch, "E109.direction1", {"start": v(0, 126) * mm, "end": v(25, 126) * mm, "construction": true});
            skLineSegment(sketch, "E109.direction2", {"start": v(0, 126) * mm, "end": v(0, 446) * mm, "construction": true});
            skSolve(sketch);
        }
        {
            var Q0;
            Q0 = qSketchRegion(id + "F34", true);
            extrude(context, id + "F35", {"entities" : qUnion([Q0]), "operationType" : NewBodyOperationType.REMOVE, "oppositeDirection" : true, "depth" : 60 * mm, "offsetDistance" : 25 * mm});
        }
        {
            var Q0;
            Q0=makeQuery(id+"F3.opExtrude","SWEPT_FACE",FACE,{"disambiguationData":[OSD([sQuery(id+"F2.wireOp",EDGE,"E12.right")])]});
            var sketch = newSketch(context, id + "F36", { "sketchPlane" : qUnion([Q0])});
            skCircle(sketch, "E110", {"center": v(0, 126) * mm, "radius": 15 * mm});
            skCircle(sketch, "E111", {"center": v(0, 1086) * mm, "radius": 15 * mm});
            skCircle(sketch, "E112", {"center": v(0, 766) * mm, "radius": 15 * mm});
            skCircle(sketch, "E113", {"center": v(0, 446) * mm, "radius": 15 * mm});
            skSolve(sketch);
        }
        {
            var Q0;
            Q0 = qSketchRegion(id + "F36", true);
            extrude(context, id + "F37", {"entities" : qUnion([Q0]), "operationType" : NewBodyOperationType.REMOVE, "oppositeDirection" : true, "depth" : 10 * mm, "offsetDistance" : 25 * mm});
        }
        {
            var Q0;
            Q0=makeQuery(id+"F28.opExtrude","CAP_FACE",FACE,{"disambiguationData":[OSD([sQuery(id+"F27.wireOp",EDGE,"E72.bottom"),sQuery(id+"F27.wireOp",EDGE,"E72.top"),sQuery(id+"F27.wireOp",EDGE,"E72.left"),sQuery(id+"F27.wireOp",EDGE,"E72.right"),sQuery(id+"F27.wireOp",EDGE,"E74.MirrorCS"),sQuery(id+"F27.wireOp",EDGE,"E75.MirrorCS"),sQuery(id+"F27.wireOp",EDGE,"E76.MirrorCS"),sQuery(id+"F27.wireOp",EDGE,"E77.MirrorCS"),sQuery(id+"F27.wireOp",EDGE,"E78.bottom"),sQuery(id+"F27.wireOp",EDGE,"E78.left"),sQuery(id+"F27.wireOp",EDGE,"E78.right"),sQuery(id+"F27.wireOp",EDGE,"E79.bottom"),sQuery(id+"F27.wireOp",EDGE,"E79.top"),sQuery(id+"F27.wireOp",EDGE,"E79.right"),sQuery(id+"F27.wireOp",EDGE,"E81.MirrorCS"),sQuery(id+"F27.wireOp",EDGE,"E82.MirrorCS"),sQuery(id+"F27.wireOp",EDGE,"E83.MirrorCS"),sQuery(id+"F27.wireOp",EDGE,"E84.MirrorCS"),sQuery(id+"F27.wireOp",EDGE,"E86.MirrorCS"),sQuery(id+"F27.wireOp",EDGE,"E87.MirrorCS"),sQuery(id+"F27.wireOp",EDGE,"E88.left"),sQuery(id+"F27.wireOp",EDGE,"E88.right")])],"isStart":true});
            cPlane(context, id + "F38", {"entities" : qUnion([Q0]), "cplaneType" : CPlaneType.OFFSET, "offset" : 0 * mm, "width" : 150 * mm, "height" : 150 * mm});
        }
        {
            var Q0;
            Q0=qCreatedBy(id+"F38.planeOp",FACE);
            var sketch = newSketch(context, id + "F39", { "sketchPlane" : qUnion([Q0])});
            skLineSegment(sketch, "E114.bottom", {"start": v(1882.9, -141) * mm, "end": v(1883, -141) * mm});
            skLineSegment(sketch, "E114.top", {"start": v(1882.9, 141) * mm, "end": v(1883, 141) * mm});
            skLineSegment(sketch, "E114.left", {"start": v(1882.9, -141) * mm, "end": v(1882.9, 141) * mm});
            skLineSegment(sketch, "E114.right", {"start": v(1883, -141) * mm, "end": v(1883, 141) * mm});
            skSolve(sketch);
        }
        {
            var Q0;
            Q0 = qSketchRegion(id + "F39", true);
            extrude(context, id + "F40", {"entities" : qUnion([Q0]), "operationType" : NewBodyOperationType.REMOVE, "endBound" : BoundingType.THROUGH_ALL, "oppositeDirection" : true, "depth" : 25 * mm, "offsetDistance" : 25 * mm});
        }
        {
            var Q0;
            Q0=qCreatedBy(id+"F38.planeOp",FACE);
            var sketch = newSketch(context, id + "F41", { "sketchPlane" : qUnion([Q0])});
            skLineSegment(sketch, "E115.bottom", {"start": v(1901.7, -168.7) * mm, "end": v(1901.6, -168.7) * mm});
            skLineSegment(sketch, "E115.top", {"start": v(1901.7, 168.7) * mm, "end": v(1901.6, 168.7) * mm});
            skLineSegment(sketch, "E115.left", {"start": v(1901.7, -168.7) * mm, "end": v(1901.7, 168.7) * mm});
            skLineSegment(sketch, "E115.right", {"start": v(1901.6, -168.7) * mm, "end": v(1901.6, 168.7) * mm});
            skLineSegment(sketch, "E116.bottom", {"start": v(1787.2, -78.93) * mm, "end": v(1787.3, -78.93) * mm});
            skLineSegment(sketch, "E116.top", {"start": v(1787.2, 85) * mm, "end": v(1787.3, 85) * mm});
            skLineSegment(sketch, "E116.left", {"start": v(1787.2, -78.93) * mm, "end": v(1787.2, 85) * mm});
            skLineSegment(sketch, "E116.right", {"start": v(1787.3, -78.93) * mm, "end": v(1787.3, 85) * mm});
            skLineSegment(sketch, "E117.bottom", {"start": v(1804.2, -204.93) * mm, "end": v(1804.3, -204.93) * mm});
            skLineSegment(sketch, "E117.top", {"start": v(1804.2, 226.76) * mm, "end": v(1804.3, 226.76) * mm});
            skLineSegment(sketch, "E117.left", {"start": v(1804.2, -204.93) * mm, "end": v(1804.2, 226.76) * mm});
            skLineSegment(sketch, "E117.right", {"start": v(1804.3, -204.93) * mm, "end": v(1804.3, 226.76) * mm});
            skSolve(sketch);
        }
        {
            var Q0;
            Q0 = qSketchRegion(id + "F41", true);
            extrude(context, id + "F42", {"entities" : qUnion([Q0]), "operationType" : NewBodyOperationType.REMOVE, "endBound" : BoundingType.THROUGH_ALL, "oppositeDirection" : true, "depth" : 25 * mm, "offsetDistance" : 25 * mm});
        }
        {
            var Q0;
            Q0=qCreatedBy(id+"F38.planeOp",FACE);
            var sketch = newSketch(context, id + "F43", { "sketchPlane" : qUnion([Q0])});
            skLineSegment(sketch, "E118.bottom", {"start": v(1882.9, -173.26) * mm, "end": v(1883, -173.26) * mm});
            skLineSegment(sketch, "E118.top", {"start": v(1882.9, 192.74) * mm, "end": v(1883, 192.74) * mm});
            skLineSegment(sketch, "E118.left", {"start": v(1882.9, -173.26) * mm, "end": v(1882.9, 192.74) * mm});
            skLineSegment(sketch, "E118.right", {"start": v(1883, -173.26) * mm, "end": v(1883, 192.74) * mm});
            skSolve(sketch);
        }
        {
            var Q0;
            Q0 = qSketchRegion(id + "F43", true);
            extrude(context, id + "F44", {"entities" : qUnion([Q0]), "operationType" : NewBodyOperationType.REMOVE, "endBound" : BoundingType.THROUGH_ALL, "oppositeDirection" : true, "depth" : 25 * mm, "offsetDistance" : 25 * mm});
        }
    });
